# Revit family: X6160-X6180 Vertical Series Automatic
name_source: partatom
category: Mechanical Equipment
units: mm (PartAtom-declared; Revit-internal decimal feet)

## family parameters
Always vertical = No
Cut with Voids When Loaded = No
OmniClass Number = 23.60.30.21
OmniClass Title = Pumps
Part Type = Normal
Room Calculation Point = No
Round Connector Dimension = Use Radius
Shared = Yes
Work Plane-Based = Yes

## types (7) — shared parameters
Assembly Code = D2010900
Cooling = Oil Filled
Cord Length = 240"
Cord Type = UL listed, 5-wire (1 Ph)
Default Elevation = 0"
Description = Commercial Effluent Pumps for Class I, Division 1, Group C & D Locations
Discharge Description = 1-1/2" NPT (optional 2" or 3" flange)
Discharge Diameter = 1 1/2"
Discharge Height = 6 1/16"
Discharge Radius = 3/4"
Height = 26 13/32"
Hertz = 60
Impeller = Bronze
Impeller Type = Non-clogging vortex
Installation Type = Floor Mounted
Insulation = Class B
Length = 13 5/16"
Manufacturer = Zoeller
Material = Cast Iron-Zoeller-Powder Coated Epoxy
Max. Operating Temp. = 104 °F
Mechanical Seals = Carbon and ceramic with stainless steel parts
Motor Protection = Auto Reset Thermal Overload
Motor Type = Submersible
Off Point = 10 3/4" Min and 20 1/2" Min
On Point = 11 3/4" Max and 21 1/2" Max
Operation = Automatic
Overall Height = 26 13/32"
Price = Prices may vary. Please consult Manufacturer Representative for most up-to-date price list.
Product Documentation Link = https://www.zoellerengineered.com
Product Page URL = https://www.zoellerengineered.com
RPM = 3450
Shipping Weight = 125-133 lbs
Solid Handling = 3/4 inches Spherical Solids
Square Ring & Gasket = Neoprene
Type = Permanent Split Capacitor or 3 Phase
Type SOW Power Cord Length = 300"
URL = http://www.zoellerengprod.com
Warranty Information = 36 Months (Limited)
Waste Connection = Yes
Width = 8"

## per-type parameters (varying)
| type | Amps | Apparent Load | Flow @ 5' | Max. Head | Model | Motor | Phase | Voltage |
| MX6161-1.5"-3" 115V/1Ph/15A/0.5HP | 15 A | 1725 VA | 58 GPM | 114" | MX6166 | 0.5 HP | 1 | 115 V |
| DX6186-1.5"-3" 230V/1Ph/13.7A/1.5HP | 14 A | 3151 VA | 58 GPM | 114" | DX6186 | 1.5 HP | 1 | 230 V |
| DX6188-1.5"-3" 230V/1Ph/14.0A/1.5HP | 14 A | 3220 VA | 145 GPM | 91" | DX6188 | 1.5 HP | 1 | 230 V |
| DX6189-1.5"-3" 230V/1Ph/17.1A/2HP | 17 A | 3933 VA | 145 GPM | 110" | DX6189 | 2 HP | 1 | 230 V |
| MX6163-1.5"-3" 115V/1Ph/15A/0.5HP | 15 A | 1725 VA | 58 GPM | 56 ft. | MX6163 | 0.5 HP | 1 | 115 V |
| HX6188-1.5”-3” 200V/1Ph/14.0A/1.5HP | 14 A | 2800 VA | 145 GPM | 91" | HX6188 | 1.5 HP | 1 | 200 V |
| HX6189-1.5”-3” 200V/1Ph/20.5A/2Hp | 21 A | 4100 VA | 145 GPM | 110" | HX6189 | 1.5 HP | 2 | 200 V |

## geometry (parser evidence)
native form markers: Sweep x4
no freeform markers — native parametric forms only
